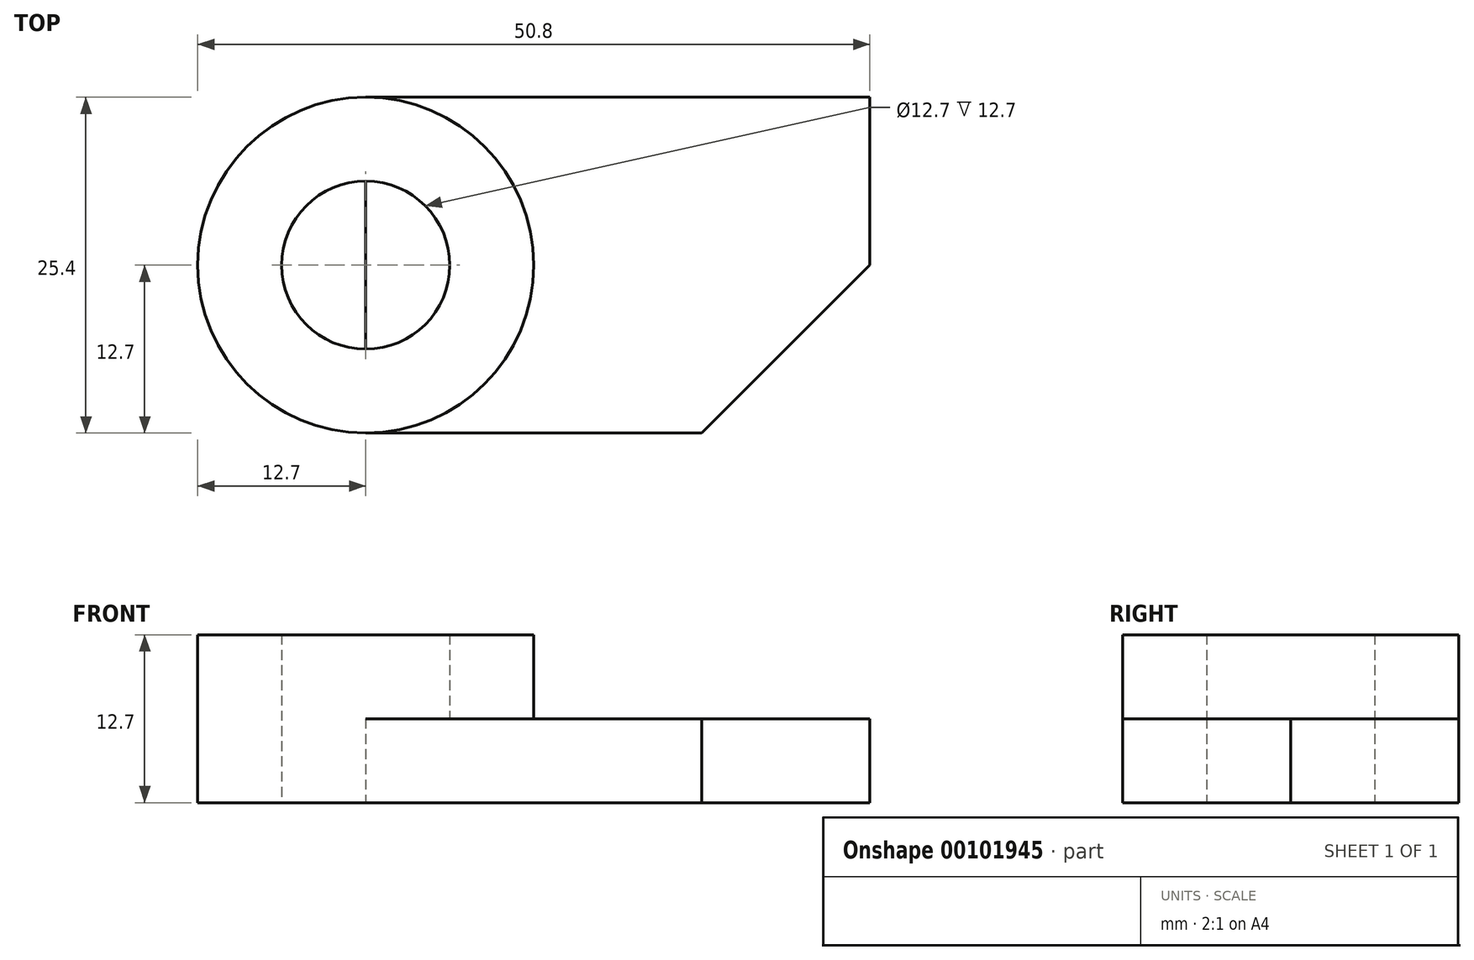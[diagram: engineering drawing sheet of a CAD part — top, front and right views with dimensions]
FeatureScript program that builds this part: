
annotation { "Feature Type Name" : "Feature", "Feature Type Description" : "" }
export const myFeature = defineFeature(function(context is Context, id is Id, definition is map)
    precondition{}
    {
        {
            var Q0;
            Q0=qCreatedBy(makeId("Top.planeOp"),FACE);
            var sketch = newSketch(context, id + "F0", { "sketchPlane" : qUnion([Q0])});
            skCircle(sketch, "E0", {"center": v(0, 0) * mm, "radius": 6.35 * mm});
            skCircle(sketch, "E1", {"center": v(0, 0) * mm, "radius": 12.7 * mm});
            skSolve(sketch);
        }
        {
            var Q0;
            Q0 = qSketchRegion(id + "F0", true);
            extrude(context, id + "F1", {"entities" : qUnion([Q0]), "endBound" : BoundingType.SYMMETRIC, "depth" : 12.7 * mm});
        }
        {
            var Q0;
            Q0=qCreatedBy(makeId("Top.planeOp"),FACE);
            var sketch = newSketch(context, id + "F2", { "sketchPlane" : qUnion([Q0])});
            skLineSegment(sketch, "E2.bottom", {"start": v(0, 12.7) * mm, "end": v(38.1, 12.7) * mm});
            skLineSegment(sketch, "E2.top", {"start": v(0, -12.7) * mm, "end": v(38.1, -12.7) * mm});
            skLineSegment(sketch, "E2.left", {"start": v(0, 12.7) * mm, "end": v(0, -12.7) * mm});
            skLineSegment(sketch, "E2.right", {"start": v(38.1, 12.7) * mm, "end": v(38.1, -12.7) * mm});
            skSolve(sketch);
        }
        {
            var Q0;
            Q0 = qSketchRegion(id + "F2", true);
            extrude(context, id + "F3", {"entities" : qUnion([Q0]), "operationType" : NewBodyOperationType.ADD, "oppositeDirection" : true, "depth" : 6.35 * mm});
        }
        {
            var Q0;
            {var subQ0=sQuery(id+"F2.wireOp",EDGE,"E2.bottom");var subQ1=sQuery(id+"F2.wireOp",EDGE,"E2.top");var subQ2=sQuery(id+"F2.wireOp",EDGE,"E2.right");Q0=makeQuery(id+"F3.boolean.opBoolean","SPLIT",FACE,{"disambiguationData":[TD([makeQuery(id+"F1.opExtrude","SWEPT_FACE",FACE,{"disambiguationData":[OSD([sQuery(id+"F0.wireOp",EDGE,"E1")])]})])],"derivedFrom":makeQuery(id+"F3.opExtrude","CAP_FACE",FACE,{"disambiguationData":[OSD([subQ0,subQ1,sQuery(id+"F2.wireOp",EDGE,"E2.left"),subQ2])],"isStart":true})});}
            var sketch = newSketch(context, id + "F4", { "sketchPlane" : qUnion([Q0])});
            skLineSegment(sketch, "E3", {"start": v(38.1, 0) * mm, "end": v(25.4, -12.7) * mm});
            skSolve(sketch);
        }
        {
            var Q0;
            {var subQ0=sQuery(id+"F4.wireOp",EDGE,"E3");Q0=makeQuery(id+"F4.imprint","IMPRINT",FACE,{"disambiguationData":[TD([[makeQuery(id+"F4.imprint","IMPRINT",EDGE,{"derivedFrom":subQ0}),1.0]])]});}
            extrude(context, id + "F5", {"entities" : qUnion([Q0]), "operationType" : NewBodyOperationType.REMOVE, "endBound" : BoundingType.THROUGH_ALL, "oppositeDirection" : true, "depth" : 25.4 * mm});
        }
    });
